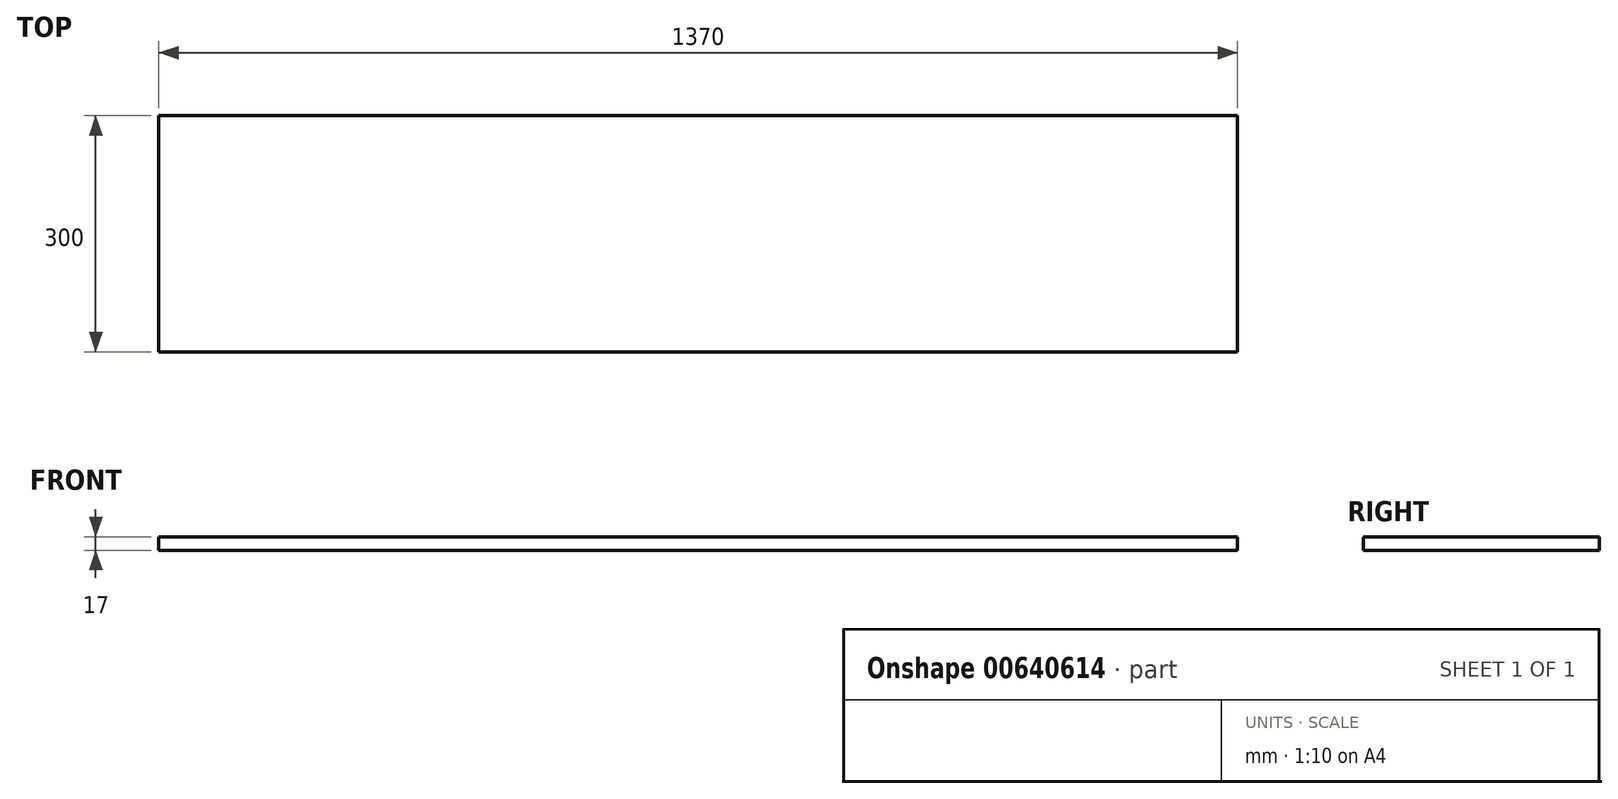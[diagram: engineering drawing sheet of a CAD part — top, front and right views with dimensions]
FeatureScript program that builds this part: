
annotation { "Feature Type Name" : "Feature", "Feature Type Description" : "" }
export const myFeature = defineFeature(function(context is Context, id is Id, definition is map)
    precondition{}
    {
        {
            var Q0;
            Q0=qCreatedBy(makeId("Top.planeOp"),FACE);
            var sketch = newSketch(context, id + "F0", { "sketchPlane" : qUnion([Q0])});
            skLineSegment(sketch, "E0.bottom", {"start": v(0, 0) * mm, "end": v(-1370, 0) * mm});
            skLineSegment(sketch, "E0.top", {"start": v(0, 300) * mm, "end": v(-1370, 300) * mm});
            skLineSegment(sketch, "E0.left", {"start": v(0, 0) * mm, "end": v(0, 300) * mm});
            skLineSegment(sketch, "E0.right", {"start": v(-1370, 0) * mm, "end": v(-1370, 300) * mm});
            skSolve(sketch);
        }
        {
            var Q0;
            Q0 = qSketchRegion(id + "F0", true);
            extrude(context, id + "F1", {"entities" : qUnion([Q0]), "depth" : 17 * mm, "offsetDistance" : 25 * mm});
        }
    });
